# Revit family: QF_ACP_AXP-MXP
name_source: partatom
category: Specialty Equipment
revit_build: Autodesk Revit 2016 (Build: 20150714_1515(x64)
units: mm (PartAtom-declared; Revit-internal decimal feet)

## family parameters
Always vertical = Yes
Cut with Voids When Loaded = No
OmniClass Number = 23.40.40.14.31
OmniClass Title = Cleaning and Disposal Equipment
Part Type = Normal
Room Calculation Point = No
Round Connector Dimension = Use Diameter
Shared = No
Work Plane-Based = Yes

## types (1)
- QF_ACP_AXP-MXP
    Apparent Power = 5699 VA
    Assembly Code = E1090320
    CSI MasterFormat = 11 44 16
    Conn Plug = NEMA 6-30P
    Cycle = 60 Hz
    Default Elevation = 48 "
    Description = Combination Cooking Oven
    FL Amps = 27 A
    Manufacturer = ACP
    Model = AXP-MXP
    Phase = 1
    URL = www.acpsolutions.com
    Volts = 208 V
    Watts = 5700 W
    Weight in Pounds = 150

## geometry (parser evidence)
native form markers: Sweep x3
no freeform markers — native parametric forms only
